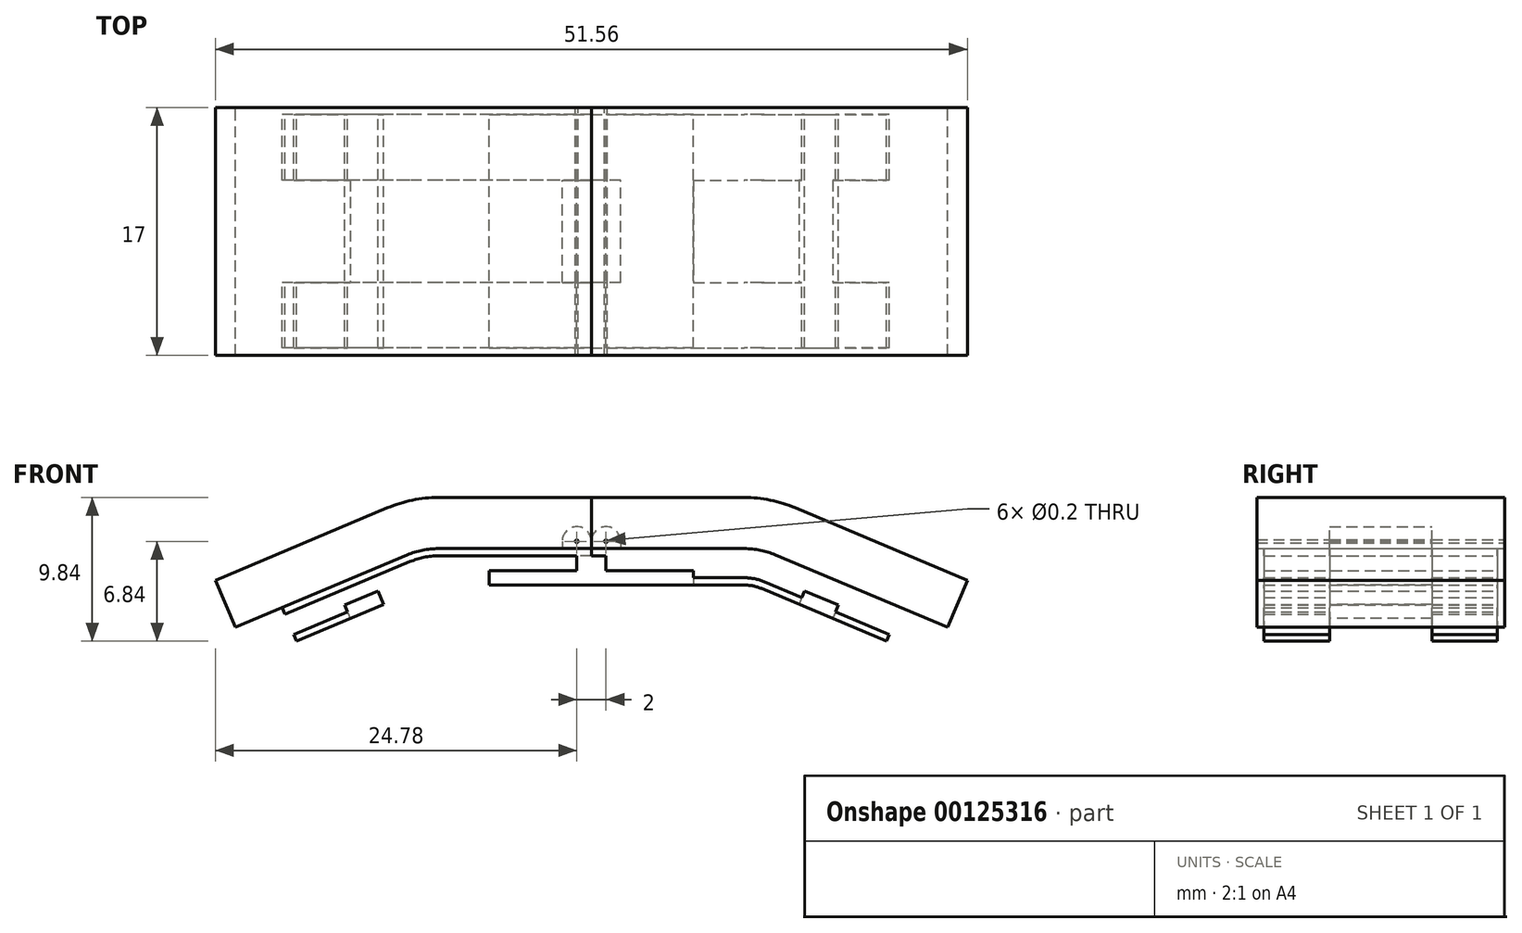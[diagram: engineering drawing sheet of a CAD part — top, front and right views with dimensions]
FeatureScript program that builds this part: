
annotation { "Feature Type Name" : "Feature", "Feature Type Description" : "" }
export const myFeature = defineFeature(function(context is Context, id is Id, definition is map)
    precondition{}
    {
        {
            var Q0;
            Q0=qCreatedBy(makeId("Front.planeOp"),FACE);
            var sketch = newSketch(context, id + "F0", { "sketchPlane" : qUnion([Q0])});
            skLineSegment(sketch, "E0", {"start": v(0, 0) * mm, "end": v(10.5, 0) * mm});
            skLineSegment(sketch, "E1", {"start": v(21, 0) * mm, "end": v(21, -3.46) * mm});
            skLineSegment(sketch, "E2", {"start": v(12.43, -0.4) * mm, "end": v(21, -4) * mm});
            skPoint(sketch, "E3.newPointA", {"position": v(21, 0) * mm});
            skArc(sketch, "E3.filletArc", {"start": v(12.43, -0.4) * mm, "mid": v(11.48, -0.1) * mm, "end": v(10.5, 0) * mm});
            skLineSegment(sketch, "E4", {"start": v(0, 0) * mm, "end": v(0, -2) * mm});
            skLineSegment(sketch, "E5.0", {"start": v(11.65, -2.24) * mm, "end": v(20.22, -5.84) * mm});
            skArc(sketch, "E5.1", {"start": v(11.65, -2.24) * mm, "mid": v(11.08, -2.06) * mm, "end": v(10.5, -2) * mm});
            skLineSegment(sketch, "E5.2", {"start": v(0, -2) * mm, "end": v(10.5, -2) * mm});
            skLineSegment(sketch, "E6", {"start": v(21, -4) * mm, "end": v(20.22, -5.84) * mm});
            skLineSegment(sketch, "E7.MirrorCS", {"start": v(0, 0) * mm, "end": v(-11.5, 0) * mm});
            skArc(sketch, "E8.MirrorCS", {"start": v(-12.43, -0.4) * mm, "mid": v(-11.48, -0.1) * mm, "end": v(-10.5, 0) * mm});
            skLineSegment(sketch, "E9.MirrorCS", {"start": v(0, -2) * mm, "end": v(-10.5, -2) * mm});
            skLineSegment(sketch, "E10.MirrorCS", {"start": v(-12.43, -0.4) * mm, "end": v(-21, -4) * mm});
            skLineSegment(sketch, "E11.MirrorCS", {"start": v(-11.65, -2.24) * mm, "end": v(-20.22, -5.84) * mm});
            skLineSegment(sketch, "E12.MirrorCS", {"start": v(-21, -4) * mm, "end": v(-20.22, -5.84) * mm});
            skArc(sketch, "E13.MirrorCS", {"start": v(-11.65, -2.24) * mm, "mid": v(-11.08, -2.06) * mm, "end": v(-10.5, -2) * mm});
            skLineSegment(sketch, "E14", {"start": v(21, -4) * mm, "end": v(14.9, -1.43) * mm});
            skLineSegment(sketch, "E15", {"start": v(21, -4) * mm, "end": v(15, -1.48) * mm});
            skLineSegment(sketch, "E16", {"start": v(14.62, -2.4) * mm, "end": v(16.93, -3.37) * mm});
            skLineSegment(sketch, "E17.MirrorCS", {"start": v(-14.62, -2.4) * mm, "end": v(-16.93, -3.37) * mm});
            skLineSegment(sketch, "E18", {"start": v(0, 0) * mm, "end": v(7, 0) * mm});
            skLineSegment(sketch, "E19", {"start": v(7, -1) * mm, "end": v(0, -1) * mm});
            skLineSegment(sketch, "E20.MirrorCS", {"start": v(-7, -1) * mm, "end": v(0, -1) * mm});
            skLineSegment(sketch, "E21", {"start": v(7, -1) * mm, "end": v(7, -2) * mm});
            skLineSegment(sketch, "E22", {"start": v(-7, -1) * mm, "end": v(-7, -2) * mm});
            skLineSegment(sketch, "E23", {"start": v(-14.62, -2.4) * mm, "end": v(-14.23, -3.32) * mm});
            skLineSegment(sketch, "E24", {"start": v(-16.93, -3.37) * mm, "end": v(-16.54, -4.3) * mm});
            skLineSegment(sketch, "E25", {"start": v(16.93, -3.37) * mm, "end": v(16.54, -4.3) * mm});
            skLineSegment(sketch, "E26", {"start": v(14.62, -2.4) * mm, "end": v(14.23, -3.32) * mm});
            skPoint(sketch, "E27.MirrorCS.start.orphan", {"position": v(-15, -1.48) * mm});
            skPoint(sketch, "E28.MirrorCS.end.orphan", {"position": v(-17.31, -2.45) * mm});
            skPoint(sketch, "E28.MirrorCS.start.orphan", {"position": v(-16.93, -3.37) * mm});
            skPoint(sketch, "E29.MirrorCS.end.orphan", {"position": v(-7, -1) * mm});
            skPoint(sketch, "E29.MirrorCS.start.orphan", {"position": v(-7, 0) * mm});
            skPoint(sketch, "E30.end.orphan", {"position": v(17.31, -2.45) * mm});
            skLineSegment(sketch, "E31", {"start": v(0, 0) * mm, "end": v(1, 0) * mm});
            skLineSegment(sketch, "E32", {"start": v(1, 0) * mm, "end": v(1, -1) * mm});
            skLineSegment(sketch, "E33.MirrorCS", {"start": v(-1, 0) * mm, "end": v(-1, -1) * mm});
            skPoint(sketch, "E34.orphan", {"position": v(11.5, 0) * mm});
            skLineSegment(sketch, "E35.0", {"start": v(2, 0.5) * mm, "end": v(7, 0.5) * mm});
            skLineSegment(sketch, "E36.0", {"start": v(2, 0.5) * mm, "end": v(10.5, 0.5) * mm});
            skArc(sketch, "E37.0", {"start": v(12.62, 0.07) * mm, "mid": v(11.58, 0.4) * mm, "end": v(10.5, 0.5) * mm});
            skLineSegment(sketch, "E38.0", {"start": v(12.62, 0.07) * mm, "end": v(21.2, -3.54) * mm});
            skLineSegment(sketch, "E39", {"start": v(20.22, -5.84) * mm, "end": v(21.2, -3.54) * mm});
            skPoint(sketch, "E40.end.orphan", {"position": v(20.76, -4.57) * mm});
            skPoint(sketch, "E40.start.orphan", {"position": v(22.72, -4.18) * mm});
            skLineSegment(sketch, "E41", {"start": v(21.2, -3.54) * mm, "end": v(20.42, -5.38) * mm});
            skLineSegment(sketch, "E42", {"start": v(20.42, -5.38) * mm, "end": v(16.73, -3.83) * mm});
            skLineSegment(sketch, "E43.0", {"start": v(11.85, -1.77) * mm, "end": v(14.43, -2.86) * mm});
            skArc(sketch, "E43.1", {"start": v(11.85, -1.77) * mm, "mid": v(11.18, -1.57) * mm, "end": v(10.5, -1.5) * mm});
            skLineSegment(sketch, "E43.2", {"start": v(7, -1.5) * mm, "end": v(10.5, -1.5) * mm});
            skLineSegment(sketch, "E44.trimOffspring", {"start": v(16.73, -3.83) * mm, "end": v(20.42, -5.38) * mm});
            skLineSegment(sketch, "E45.MirrorCS", {"start": v(-2, 0.5) * mm, "end": v(-7, 0.5) * mm});
            skLineSegment(sketch, "E46.MirrorCS", {"start": v(-2, 0.5) * mm, "end": v(-10.5, 0.5) * mm});
            skArc(sketch, "E47.MirrorCS", {"start": v(-12.62, 0.07) * mm, "mid": v(-11.58, 0.4) * mm, "end": v(-10.5, 0.5) * mm});
            skLineSegment(sketch, "E48.MirrorCS", {"start": v(-12.62, 0.07) * mm, "end": v(-21.2, -3.54) * mm});
            skLineSegment(sketch, "E49.MirrorCS", {"start": v(-20.22, -5.84) * mm, "end": v(-21.2, -3.54) * mm});
            skLineSegment(sketch, "E50.MirrorCS", {"start": v(-20.42, -5.38) * mm, "end": v(-16.73, -3.83) * mm});
            skLineSegment(sketch, "E51.MirrorCS", {"start": v(-11.85, -1.77) * mm, "end": v(-14.43, -2.86) * mm});
            skArc(sketch, "E52.MirrorCS", {"start": v(-11.85, -1.77) * mm, "mid": v(-11.18, -1.57) * mm, "end": v(-10.5, -1.5) * mm});
            skLineSegment(sketch, "E53.MirrorCS", {"start": v(-7, -1.5) * mm, "end": v(-10.5, -1.5) * mm});
            skLineSegment(sketch, "E54", {"start": v(7, -1.5) * mm, "end": v(1, -1.5) * mm});
            skLineSegment(sketch, "E55", {"start": v(1, -1.5) * mm, "end": v(1, -1) * mm});
            skLineSegment(sketch, "E56", {"start": v(21.2, -3.54) * mm, "end": v(20.8, -4.46) * mm});
            skCircle(sketch, "E57", {"center": v(20.35, -4.27) * mm, "radius": 0.1 * mm});
            skCircle(sketch, "E58.MirrorC", {"center": v(-20.35, -4.27) * mm, "radius": 0.1 * mm});
            skLineSegment(sketch, "E59", {"start": v(1, -1.5) * mm, "end": v(1, 0) * mm});
            skLineSegment(sketch, "E60", {"start": v(2, 2) * mm, "end": v(2, 2) * mm});
            skPoint(sketch, "E61.visualSharp", {"position": v(1, 2) * mm});
            skPoint(sketch, "E62.visualSharp", {"position": v(3, 2) * mm});
            skLineSegment(sketch, "E63", {"start": v(0, 0) * mm, "end": v(0, 1) * mm});
            skLineSegment(sketch, "E64", {"start": v(1, 2) * mm, "end": v(1, 2) * mm});
            skLineSegment(sketch, "E65", {"start": v(0, 2) * mm, "end": v(0, 1.09) * mm});
            skLineSegment(sketch, "E66", {"start": v(0, 1.09) * mm, "end": v(0, 2) * mm});
            skLineSegment(sketch, "E67", {"start": v(2, 1) * mm, "end": v(2, 0.5) * mm});
            skLineSegment(sketch, "E68", {"start": v(0, 1) * mm, "end": v(0, 0) * mm});
            skPoint(sketch, "E69.visualSharp", {"position": v(0, 2) * mm});
            skArc(sketch, "E69.filletArc", {"start": v(1, 2) * mm, "mid": v(0.3, 1.7) * mm, "end": v(0, 1) * mm});
            skPoint(sketch, "E70.visualSharp", {"position": v(2, 2) * mm});
            skArc(sketch, "E70.filletArc", {"start": v(2, 1) * mm, "mid": v(1.7, 1.7) * mm, "end": v(1, 2) * mm});
            skPoint(sketch, "E71.orphan", {"position": v(1, 0.5) * mm});
            skLineSegment(sketch, "E72.MirrorCS", {"start": v(-2, 1) * mm, "end": v(-2, 0.5) * mm});
            skArc(sketch, "E73.MirrorCS", {"start": v(-2, 1) * mm, "mid": v(-1.7, 1.7) * mm, "end": v(-1, 2) * mm});
            skArc(sketch, "E74.MirrorCS", {"start": v(-1, 2) * mm, "mid": v(-0.3, 1.7) * mm, "end": v(0, 1) * mm});
            skPoint(sketch, "E75.start.orphan", {"position": v(-1, 0.5) * mm});
            skCircle(sketch, "E76", {"center": v(1, 1) * mm, "radius": 0.1 * mm});
            skCircle(sketch, "E77.MirrorC", {"center": v(-1, 1) * mm, "radius": 0.1 * mm});
            skLineSegment(sketch, "E78", {"start": v(2, 0.5) * mm, "end": v(2, 1) * mm});
            skLineSegment(sketch, "E79", {"start": v(2, 4) * mm, "end": v(0, 4) * mm});
            skLineSegment(sketch, "E80", {"start": v(0, 4) * mm, "end": v(0, 1.09) * mm});
            skLineSegment(sketch, "E81", {"start": v(0, 4) * mm, "end": v(0, 1) * mm});
            skLineSegment(sketch, "E82", {"start": v(0, 4) * mm, "end": v(7, 4) * mm});
            skLineSegment(sketch, "E83.0", {"start": v(13.98, 3.3) * mm, "end": v(22.55, -0.31) * mm});
            skArc(sketch, "E83.1", {"start": v(13.98, 3.3) * mm, "mid": v(12.27, 3.82) * mm, "end": v(10.5, 4) * mm});
            skLineSegment(sketch, "E83.2", {"start": v(2, 4) * mm, "end": v(10.5, 4) * mm});
            skLineSegment(sketch, "E84", {"start": v(21.2, -3.54) * mm, "end": v(22.55, -0.31) * mm});
            skLineSegment(sketch, "E85", {"start": v(2, 0.5) * mm, "end": v(-2, 0.5) * mm});
            skSolve(sketch);
        }
        {
            var Q0;
            {var subQ5=sQuery(id+"F0.wireOp",EDGE,"E42");Q0=makeQuery(id+"F0.imprint","IMPRINT",FACE,{"disambiguationData":[TD([[makeQuery(id+"F0.imprint","IMPRINT",EDGE,{"derivedFrom":subQ5}),1.0]])]});}
            var Q1;
            {var subQ5=sQuery(id+"F0.wireOp",EDGE,"E3.filletArc");Q1=makeQuery(id+"F0.imprint","IMPRINT",FACE,{"disambiguationData":[TD([[makeQuery(id+"F0.imprint","IMPRINT",EDGE,{"derivedFrom":subQ5}),1.0]])]});}
            var Q2;
            {var subQ4=sQuery(id+"F0.wireOp",EDGE,"E16");Q2=makeQuery(id+"F0.imprint","IMPRINT",FACE,{"disambiguationData":[TD([[makeQuery(id+"F0.imprint","IMPRINT",EDGE,{"derivedFrom":subQ4}),-1.0]])]});}
            var Q3;
            {var subQ1=sQuery(id+"F0.wireOp",EDGE,"E5.1");Q3=makeQuery(id+"F0.imprint","IMPRINT",FACE,{"disambiguationData":[TD([[makeQuery(id+"F0.imprint","IMPRINT",EDGE,{"derivedFrom":subQ1}),-1.0]])]});}
            var Q4;
            {var subQ0=sQuery(id+"F0.wireOp",EDGE,"E54");Q4=makeQuery(id+"F0.imprint","IMPRINT",FACE,{"disambiguationData":[TD([[makeQuery(id+"F0.imprint","IMPRINT",EDGE,{"derivedFrom":subQ0}),1.0]])]});}
            var Q5;
            {var subQ0=sQuery(id+"F0.wireOp",EDGE,"E32");Q5=makeQuery(id+"F0.imprint","IMPRINT",FACE,{"disambiguationData":[TD([[makeQuery(id+"F0.imprint","IMPRINT",EDGE,{"derivedFrom":subQ0}),-1.0]])]});}
            var Q6;
            {var subQ4=sQuery(id+"F0.wireOp",EDGE,"E54");Q6=makeQuery(id+"F0.imprint","IMPRINT",FACE,{"disambiguationData":[TD([[makeQuery(id+"F0.imprint","IMPRINT",EDGE,{"derivedFrom":subQ4}),-1.0]])]});}
            var Q7;
            {var subQ5=sQuery(id+"F0.wireOp",EDGE,"E33.MirrorCS");Q7=makeQuery(id+"F0.imprint","IMPRINT",FACE,{"disambiguationData":[TD([[makeQuery(id+"F0.imprint","IMPRINT",EDGE,{"derivedFrom":subQ5}),1.0]])]});}
            var Q8;
            {var subQ0=sQuery(id+"F0.wireOp",EDGE,"E20.MirrorCS");var subQ4=sQuery(id+"F0.wireOp",EDGE,"E22");var subQ5=makeQuery(id+"F0.imprint","INTERSECT",VERTEX,{"derivedFrom":[subQ0,subQ4]});Q8=makeQuery(id+"F0.imprint","IMPRINT",FACE,{"disambiguationData":[TD([[makeQuery(id+"F0.imprint","IMPRINT",EDGE,{"disambiguationData":[TD([[subQ5,-1.0]])],"derivedFrom":subQ0}),-1.0]])]});}
            var Q9;
            {var subQ3=sQuery(id+"F0.wireOp",EDGE,"E8.MirrorCS");Q9=makeQuery(id+"F0.imprint","IMPRINT",FACE,{"disambiguationData":[TD([[makeQuery(id+"F0.imprint","IMPRINT",EDGE,{"derivedFrom":subQ3}),-1.0]])]});}
            var Q10;
            {var subQ4=sQuery(id+"F0.wireOp",EDGE,"E13.MirrorCS");Q10=makeQuery(id+"F0.imprint","IMPRINT",FACE,{"disambiguationData":[TD([[makeQuery(id+"F0.imprint","IMPRINT",EDGE,{"derivedFrom":subQ4}),1.0]])]});}
            var Q11;
            {var subQ4=sQuery(id+"F0.wireOp",EDGE,"E17.MirrorCS");Q11=makeQuery(id+"F0.imprint","IMPRINT",FACE,{"disambiguationData":[TD([[makeQuery(id+"F0.imprint","IMPRINT",EDGE,{"derivedFrom":subQ4}),1.0]])]});}
            var Q12;
            {var subQ5=sQuery(id+"F0.wireOp",EDGE,"E50.MirrorCS");Q12=makeQuery(id+"F0.imprint","IMPRINT",FACE,{"disambiguationData":[TD([[makeQuery(id+"F0.imprint","IMPRINT",EDGE,{"derivedFrom":subQ5}),-1.0]])]});}
            extrude(context, id + "F1", {"entities" : qUnion([Q0, Q1, Q2, Q3, Q4, Q5, Q6, Q7, Q8, Q9, Q10, Q11, Q12]), "depth" : 16 * mm, "offsetDistance" : 25 * mm, "symmetric" : true});
        }
        {
            var Q0;
            {var subQ2=sQuery(id+"F0.wireOp",EDGE,"E8.MirrorCS");Q0=makeQuery(id+"F0.imprint","IMPRINT",FACE,{"disambiguationData":[TD([[makeQuery(id+"F0.imprint","IMPRINT",EDGE,{"derivedFrom":subQ2}),-1.0]])]});}
            var Q1;
            {var subQ5=sQuery(id+"F0.wireOp",EDGE,"E3.filletArc");Q1=makeQuery(id+"F0.imprint","IMPRINT",FACE,{"disambiguationData":[TD([[makeQuery(id+"F0.imprint","IMPRINT",EDGE,{"derivedFrom":subQ5}),1.0]])]});}
            var Q2;
            {var subQ5=sQuery(id+"F0.wireOp",EDGE,"E42");Q2=makeQuery(id+"F0.imprint","IMPRINT",FACE,{"disambiguationData":[TD([[makeQuery(id+"F0.imprint","IMPRINT",EDGE,{"derivedFrom":subQ5}),1.0]])]});}
            var Q3;
            {var subQ1=sQuery(id+"F0.wireOp",EDGE,"E5.1");Q3=makeQuery(id+"F0.imprint","IMPRINT",FACE,{"disambiguationData":[TD([[makeQuery(id+"F0.imprint","IMPRINT",EDGE,{"derivedFrom":subQ1}),-1.0]])]});}
            var Q4;
            {var subQ4=sQuery(id+"F0.wireOp",EDGE,"E13.MirrorCS");Q4=makeQuery(id+"F0.imprint","IMPRINT",FACE,{"disambiguationData":[TD([[makeQuery(id+"F0.imprint","IMPRINT",EDGE,{"derivedFrom":subQ4}),1.0]])]});}
            var Q5;
            {var subQ5=sQuery(id+"F0.wireOp",EDGE,"E50.MirrorCS");Q5=makeQuery(id+"F0.imprint","IMPRINT",FACE,{"disambiguationData":[TD([[makeQuery(id+"F0.imprint","IMPRINT",EDGE,{"derivedFrom":subQ5}),-1.0]])]});}
            extrude(context, id + "F2", {"entities" : qUnion([Q0, Q1, Q2, Q3, Q4, Q5]), "operationType" : NewBodyOperationType.REMOVE, "oppositeDirection" : true, "depth" : 7 * mm, "offsetDistance" : 25 * mm, "symmetric" : true});
        }
        {
            var Q0;
            {var subQ5=sQuery(id+"F0.wireOp",EDGE,"E3.filletArc");Q0=makeQuery(id+"F0.imprint","IMPRINT",FACE,{"disambiguationData":[TD([[makeQuery(id+"F0.imprint","IMPRINT",EDGE,{"derivedFrom":subQ5}),1.0]])]});}
            var Q1;
            {var subQ1=sQuery(id+"F0.wireOp",EDGE,"E3.filletArc");Q1=makeQuery(id+"F0.imprint","IMPRINT",FACE,{"disambiguationData":[TD([[makeQuery(id+"F0.imprint","IMPRINT",EDGE,{"derivedFrom":subQ1}),-1.0]])]});}
            var Q2;
            {var subQ1=sQuery(id+"F0.wireOp",EDGE,"E67");Q2=makeQuery(id+"F0.imprint","IMPRINT",FACE,{"disambiguationData":[TD([[makeQuery(id+"F0.imprint","IMPRINT",EDGE,{"derivedFrom":subQ1}),-1.0]])]});}
            extrude(context, id + "F3", {"entities" : qUnion([Q0, Q1, Q2]), "depth" : 7 * mm, "offsetDistance" : 25 * mm, "symmetric" : true});
        }
        {
            var Q0;
            Q0=makeQuery(id+"F3.opExtrude","SWEPT_BODY",BODY,{"disambiguationData":[OSD([sQuery(id+"F0.wireOp",EDGE,"E0"),sQuery(id+"F0.wireOp",EDGE,"E6"),sQuery(id+"F0.wireOp",EDGE,"E16"),sQuery(id+"F0.wireOp",EDGE,"E19"),sQuery(id+"F0.wireOp",EDGE,"E21"),sQuery(id+"F0.wireOp",EDGE,"E25"),sQuery(id+"F0.wireOp",EDGE,"E26"),sQuery(id+"F0.wireOp",EDGE,"E32"),sQuery(id+"F0.wireOp",EDGE,"E35.0"),sQuery(id+"F0.wireOp",EDGE,"E36.0"),sQuery(id+"F0.wireOp",EDGE,"E37.0"),sQuery(id+"F0.wireOp",EDGE,"E38.0"),sQuery(id+"F0.wireOp",EDGE,"E39"),sQuery(id+"F0.wireOp",EDGE,"E42"),sQuery(id+"F0.wireOp",EDGE,"E43.0"),sQuery(id+"F0.wireOp",EDGE,"E43.1"),sQuery(id+"F0.wireOp",EDGE,"E43.2"),sQuery(id+"F0.wireOp",EDGE,"E57"),sQuery(id+"F0.wireOp",EDGE,"E63"),sQuery(id+"F0.wireOp",EDGE,"E67"),sQuery(id+"F0.wireOp",EDGE,"E69.filletArc"),sQuery(id+"F0.wireOp",EDGE,"E70.filletArc"),sQuery(id+"F0.wireOp",EDGE,"E76")])]});
            var Q1;
            Q1=qCreatedBy(makeId("Right.planeOp"),FACE);
            mirror(context, id + "F4", {"entities" : qUnion([Q0]), "mirrorPlane" : qUnion([Q1])});
        }
        {
            var Q0;
            Q0=makeQuery(id+"F0.imprint","IMPRINT",FACE,{"disambiguationData":[TD([[makeQuery(id+"F0.imprint","IMPRINT",EDGE,{"derivedFrom":sQuery(id+"F0.wireOp",EDGE,"E35.0")}),1.0]])]});
            var Q1;
            {var subQ1=sQuery(id+"F0.wireOp",EDGE,"E67");Q1=makeQuery(id+"F0.imprint","IMPRINT",FACE,{"disambiguationData":[TD([[makeQuery(id+"F0.imprint","IMPRINT",EDGE,{"derivedFrom":subQ1}),-1.0]])]});}
            extrude(context, id + "F5", {"entities" : qUnion([Q0, Q1]), "depth" : 17 * mm, "offsetDistance" : 25 * mm, "symmetric" : true});
        }
        {
            var Q0;
            Q0=makeQuery(id+"F3.opExtrude","SWEPT_BODY",BODY,{"disambiguationData":[OSD([sQuery(id+"F0.wireOp",EDGE,"E0"),sQuery(id+"F0.wireOp",EDGE,"E6"),sQuery(id+"F0.wireOp",EDGE,"E16"),sQuery(id+"F0.wireOp",EDGE,"E19"),sQuery(id+"F0.wireOp",EDGE,"E21"),sQuery(id+"F0.wireOp",EDGE,"E25"),sQuery(id+"F0.wireOp",EDGE,"E26"),sQuery(id+"F0.wireOp",EDGE,"E32"),sQuery(id+"F0.wireOp",EDGE,"E35.0"),sQuery(id+"F0.wireOp",EDGE,"E36.0"),sQuery(id+"F0.wireOp",EDGE,"E37.0"),sQuery(id+"F0.wireOp",EDGE,"E38.0"),sQuery(id+"F0.wireOp",EDGE,"E39"),sQuery(id+"F0.wireOp",EDGE,"E42"),sQuery(id+"F0.wireOp",EDGE,"E43.0"),sQuery(id+"F0.wireOp",EDGE,"E43.1"),sQuery(id+"F0.wireOp",EDGE,"E43.2"),sQuery(id+"F0.wireOp",EDGE,"E57"),sQuery(id+"F0.wireOp",EDGE,"E63"),sQuery(id+"F0.wireOp",EDGE,"E67"),sQuery(id+"F0.wireOp",EDGE,"E69.filletArc"),sQuery(id+"F0.wireOp",EDGE,"E70.filletArc"),sQuery(id+"F0.wireOp",EDGE,"E76")])]});
            var Q1;
            Q1=makeQuery(id+"F5.opExtrude","SWEPT_BODY",BODY,{"disambiguationData":[OSD([sQuery(id+"F0.wireOp",EDGE,"E35.0"),sQuery(id+"F0.wireOp",EDGE,"E36.0"),sQuery(id+"F0.wireOp",EDGE,"E37.0"),sQuery(id+"F0.wireOp",EDGE,"E38.0"),sQuery(id+"F0.wireOp",EDGE,"E63"),sQuery(id+"F0.wireOp",EDGE,"E65"),sQuery(id+"F0.wireOp",EDGE,"E76"),sQuery(id+"F0.wireOp",EDGE,"E79"),sQuery(id+"F0.wireOp",EDGE,"E80"),sQuery(id+"F0.wireOp",EDGE,"E81"),sQuery(id+"F0.wireOp",EDGE,"E82"),sQuery(id+"F0.wireOp",EDGE,"E83.0"),sQuery(id+"F0.wireOp",EDGE,"E83.1"),sQuery(id+"F0.wireOp",EDGE,"E83.2"),sQuery(id+"F0.wireOp",EDGE,"E84"),sQuery(id+"F0.wireOp",EDGE,"E85")])]});
            booleanBodies(context, id + "F6", {"operationType" : BooleanOperationType.SUBTRACTION, "tools" : qUnion([Q0]), "targets" : qUnion([Q1]), "keepTools" : true});
        }
        {
            var Q0;
            Q0=makeQuery(id+"F5.opExtrude","SWEPT_FACE",FACE,{"disambiguationData":[OSD([sQuery(id+"F0.wireOp",EDGE,"E84")])]});
            extrude(context, id + "F7", {"entities" : qUnion([Q0]), "operationType" : NewBodyOperationType.ADD, "depth" : 3.5 * mm, "offsetDistance" : 25 * mm});
        }
        {
            var Q0;
            Q0=makeQuery(id+"F5.opExtrude","SWEPT_BODY",BODY,{"disambiguationData":[OSD([sQuery(id+"F0.wireOp",EDGE,"E35.0"),sQuery(id+"F0.wireOp",EDGE,"E36.0"),sQuery(id+"F0.wireOp",EDGE,"E37.0"),sQuery(id+"F0.wireOp",EDGE,"E38.0"),sQuery(id+"F0.wireOp",EDGE,"E63"),sQuery(id+"F0.wireOp",EDGE,"E65"),sQuery(id+"F0.wireOp",EDGE,"E76"),sQuery(id+"F0.wireOp",EDGE,"E79"),sQuery(id+"F0.wireOp",EDGE,"E80"),sQuery(id+"F0.wireOp",EDGE,"E81"),sQuery(id+"F0.wireOp",EDGE,"E82"),sQuery(id+"F0.wireOp",EDGE,"E83.0"),sQuery(id+"F0.wireOp",EDGE,"E83.1"),sQuery(id+"F0.wireOp",EDGE,"E83.2"),sQuery(id+"F0.wireOp",EDGE,"E84"),sQuery(id+"F0.wireOp",EDGE,"E85")])]});
            var Q1;
            Q1=qCreatedBy(makeId("Right.planeOp"),FACE);
            mirror(context, id + "F8", {"entities" : qUnion([Q0]), "mirrorPlane" : qUnion([Q1])});
        }
    });
